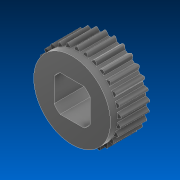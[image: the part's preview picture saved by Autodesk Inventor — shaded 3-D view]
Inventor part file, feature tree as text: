
AUTODESK INVENTOR PART (.ipt)
format: ipt  version: 2022 (Build 260153000, 153)  size: 333,312 bytes
history: native  units: in
note: dims shown in document units (in); Inventor stores cm internally (conversion verified against a paired STEP export)
features: sketch x4, extrude x3, other x3, reference x1, projected_geometry x1
ambient origin geometry x8: Origin, YZ Plane, XZ Plane, XY Plane, X Axis, Y Axis, Z Axis, Center Point
bodies: Solid1 (feature_tree)
feature tree (12):
  sketch  "Sketch1"  dims[d0=0.25in d1=0.3in]
  extrude  "Extrusion1"  Depth=0.25in
  extrude  "Extrusion2"  Depth=0.5352in
  extrude  "Extrusion3"  Depth=0.2in TaperAngle=0.0deg
  sketch  "Sketch2"  dims[d2=0.15in d3=0.5352in]
  sketch  "Sketch3"  dims[d4=0.25in d5=0.0in d6=0.2in d7=0.0in]
  reference  "Reference1"
  sketch  "Sketch4"  dims[d8=0.001in d9=0.0in d10=0.0in]
  projected_geometry  "Projected Loop1"
  other  "Tracking Wheel Assembly.iam"
  other  "VersaPlanetary Integrated Encoder (217-5046):1"
  other  "217-4783-005 Rev7_40t_spur_REF_14deg_3"
